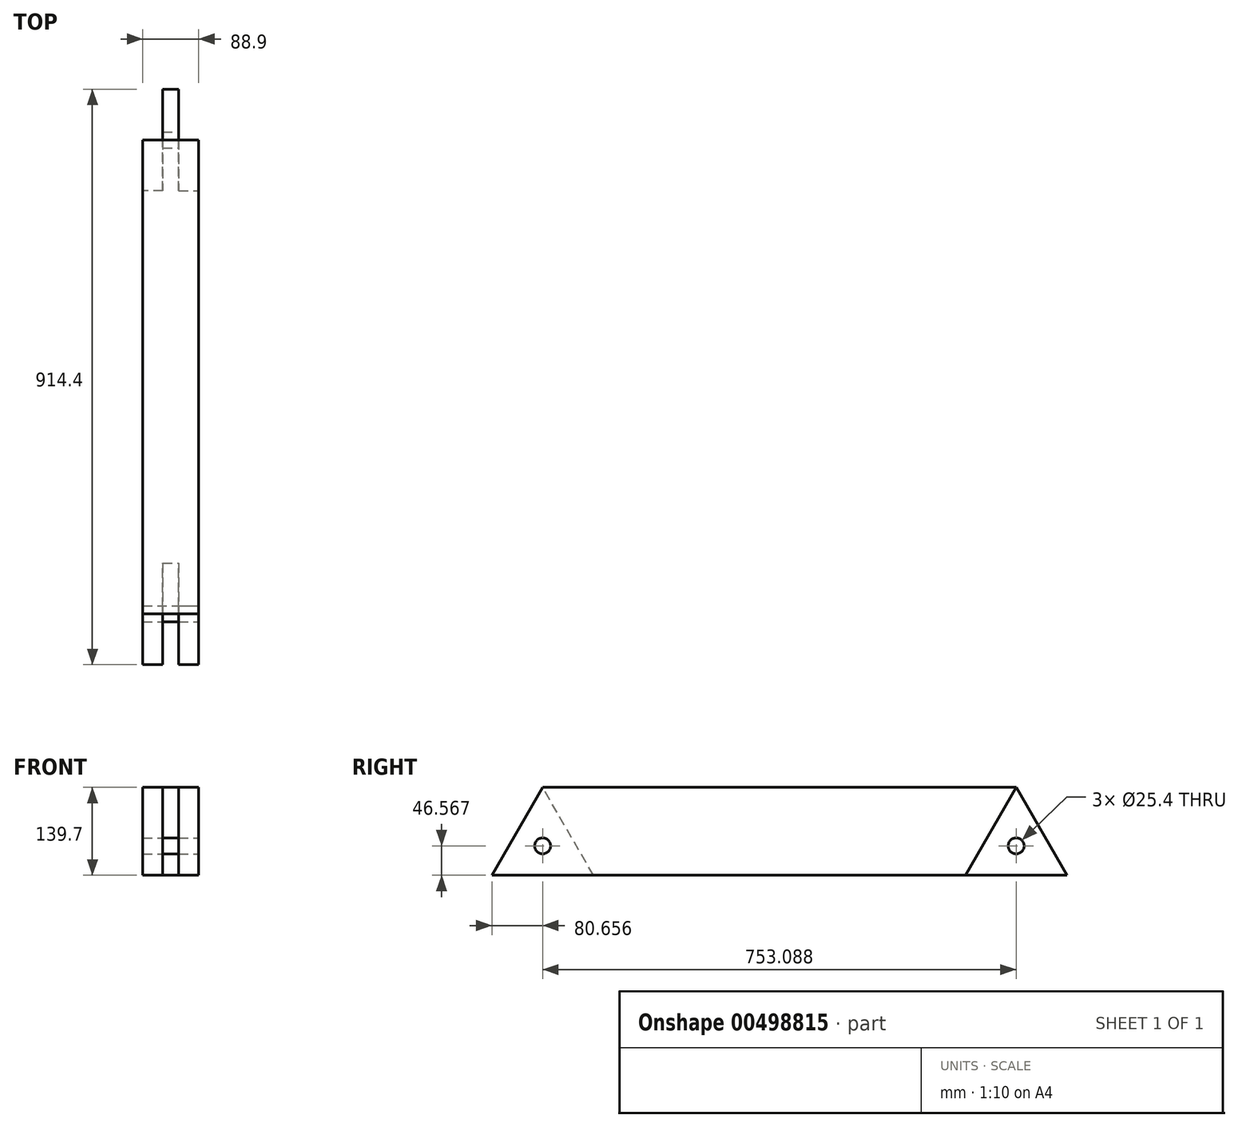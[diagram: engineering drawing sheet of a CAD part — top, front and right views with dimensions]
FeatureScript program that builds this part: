
annotation { "Feature Type Name" : "Feature", "Feature Type Description" : "" }
export const myFeature = defineFeature(function(context is Context, id is Id, definition is map)
    precondition{}
    {
        {
            var Q0;
            Q0=qCreatedBy(makeId("Right.planeOp"),FACE);
            var sketch = newSketch(context, id + "F0", { "sketchPlane" : qUnion([Q0])});
            skLineSegment(sketch, "E0.bottom", {"start": v(-376.54, 69.85) * mm, "end": v(376.54, 69.85) * mm});
            skLineSegment(sketch, "E0.top", {"start": v(-457.2, -69.85) * mm, "end": v(457.2, -69.85) * mm});
            skLineSegment(sketch, "E1", {"start": v(-457.2, -69.85) * mm, "end": v(-376.54, 69.85) * mm});
            skLineSegment(sketch, "E2", {"start": v(376.54, 69.85) * mm, "end": v(457.2, -69.85) * mm});
            skLineSegment(sketch, "E3", {"start": v(-376.54, 69.85) * mm, "end": v(-295.89, -69.85) * mm, "construction": true});
            skLineSegment(sketch, "E4", {"start": v(-295.89, -69.85) * mm, "end": v(-457.2, -69.85) * mm, "construction": true});
            skSolve(sketch);
        }
        {
            var Q0;
            Q0=makeQuery(id+"F0.imprint","IMPRINT",FACE,{"disambiguationData":[TD([[makeQuery(id+"F0.imprint","IMPRINT",EDGE,{"derivedFrom":sQuery(id+"F0.wireOp",EDGE,"E0.bottom")}),-1.0]])]});
            extrude(context, id + "F1", {"entities" : qUnion([Q0]), "depth" : 44.45 * mm, "hasSecondDirection" : true, "secondDirectionOppositeDirection" : true, "secondDirectionDepth" : 44.45 * mm});
        }
        {
            var Q0;
            Q0=qCreatedBy(makeId("Right.planeOp"),FACE);
            var sketch = newSketch(context, id + "F2", { "sketchPlane" : qUnion([Q0])});
            skLineSegment(sketch, "E5", {"start": v(-376.54, 69.85) * mm, "end": v(-457.2, -69.85) * mm});
            skLineSegment(sketch, "E6", {"start": v(-457.2, -69.85) * mm, "end": v(-295.89, -69.85) * mm});
            skLineSegment(sketch, "E7", {"start": v(-295.89, -69.85) * mm, "end": v(-376.54, 69.85) * mm});
            skSolve(sketch);
        }
        {
            var Q0;
            Q0 = qSketchRegion(id + "F2", true);
            extrude(context, id + "F3", {"entities" : qUnion([Q0]), "operationType" : NewBodyOperationType.REMOVE, "oppositeDirection" : true, "depth" : 12.7 * mm, "hasSecondDirection" : true, "secondDirectionOppositeDirection" : false, "secondDirectionDepth" : 12.7 * mm});
        }
        {
            var Q0;
            Q0=makeQuery(id+"F1.opExtrude","CAP_FACE",FACE,{"disambiguationData":[OSD([sQuery(id+"F0.wireOp",EDGE,"E0.bottom"),sQuery(id+"F0.wireOp",EDGE,"E0.top"),sQuery(id+"F0.wireOp",EDGE,"E1"),sQuery(id+"F0.wireOp",EDGE,"E2")])],"isStart":false});
            var sketch = newSketch(context, id + "F4", { "sketchPlane" : qUnion([Q0])});
            skLineSegment(sketch, "E8", {"start": v(376.54, 69.85) * mm, "end": v(457.2, -69.85) * mm});
            skLineSegment(sketch, "E9", {"start": v(376.54, 69.85) * mm, "end": v(295.89, -69.85) * mm});
            skLineSegment(sketch, "E10", {"start": v(295.89, -69.85) * mm, "end": v(457.2, -69.85) * mm});
            skSolve(sketch);
        }
        {
            var Q0;
            Q0 = qSketchRegion(id + "F4", true);
            extrude(context, id + "F5", {"entities" : qUnion([Q0]), "operationType" : NewBodyOperationType.REMOVE, "oppositeDirection" : true, "depth" : 31.75 * mm});
        }
        {
            var Q0;
            Q0=makeQuery(id+"F1.opExtrude","CAP_FACE",FACE,{"disambiguationData":[OSD([sQuery(id+"F0.wireOp",EDGE,"E0.bottom"),sQuery(id+"F0.wireOp",EDGE,"E0.top"),sQuery(id+"F0.wireOp",EDGE,"E1"),sQuery(id+"F0.wireOp",EDGE,"E2")])],"isStart":true});
            var sketch = newSketch(context, id + "F6", { "sketchPlane" : qUnion([Q0])});
            skLineSegment(sketch, "E11", {"start": v(-376.54, 69.85) * mm, "end": v(-457.2, -69.85) * mm});
            skLineSegment(sketch, "E12", {"start": v(-376.54, 69.85) * mm, "end": v(-295.89, -69.85) * mm});
            skLineSegment(sketch, "E13", {"start": v(-295.89, -69.85) * mm, "end": v(-457.2, -69.85) * mm});
            skSolve(sketch);
        }
        {
            var Q0;
            Q0 = qSketchRegion(id + "F6", true);
            extrude(context, id + "F7", {"entities" : qUnion([Q0]), "operationType" : NewBodyOperationType.REMOVE, "oppositeDirection" : true, "depth" : 31.75 * mm});
        }
        {
            var Q0;
            Q0=qCreatedBy(makeId("Right.planeOp"),FACE);
            var sketch = newSketch(context, id + "F8", { "sketchPlane" : qUnion([Q0])});
            skLineSegment(sketch, "E14", {"start": v(-376.54, 69.85) * mm, "end": v(-457.2, -69.85) * mm, "construction": true});
            skLineSegment(sketch, "E15", {"start": v(-457.2, -69.85) * mm, "end": v(-295.89, -69.85) * mm, "construction": true});
            skLineSegment(sketch, "E16", {"start": v(-295.89, -69.85) * mm, "end": v(-376.54, 69.85) * mm, "construction": true});
            skLineSegment(sketch, "E17", {"start": v(-376.54, 69.85) * mm, "end": v(-376.54, -69.85) * mm, "construction": true});
            skLineSegment(sketch, "E18", {"start": v(-457.2, -69.85) * mm, "end": v(-336.22, 0) * mm, "construction": true});
            skCircle(sketch, "E19", {"center": v(-376.54, -23.28) * mm, "radius": 12.7 * mm});
            skLineSegment(sketch, "E20", {"start": v(457.2, -69.85) * mm, "end": v(376.54, 69.85) * mm, "construction": true});
            skLineSegment(sketch, "E21", {"start": v(376.54, 69.85) * mm, "end": v(295.89, -69.85) * mm, "construction": true});
            skLineSegment(sketch, "E22", {"start": v(295.89, -69.85) * mm, "end": v(457.2, -69.85) * mm, "construction": true});
            skLineSegment(sketch, "E23", {"start": v(457.2, -69.85) * mm, "end": v(336.22, 0) * mm, "construction": true});
            skLineSegment(sketch, "E24", {"start": v(376.54, 69.85) * mm, "end": v(376.54, -69.85) * mm, "construction": true});
            skCircle(sketch, "E25", {"center": v(376.54, -23.28) * mm, "radius": 12.7 * mm});
            skSolve(sketch);
        }
        {
            var Q0;
            Q0 = qSketchRegion(id + "F8", true);
            extrude(context, id + "F9", {"entities" : qUnion([Q0]), "operationType" : NewBodyOperationType.REMOVE, "endBound" : BoundingType.THROUGH_ALL, "oppositeDirection" : true, "depth" : 25.4 * mm, "hasSecondDirection" : true, "secondDirectionBound" : BoundingType.THROUGH_ALL, "secondDirectionOppositeDirection" : false, "secondDirectionDepth" : 25.4 * mm});
        }
        {
            var Q0;
            Q0=makeQuery(id+"F1.opExtrude","CAP_FACE",FACE,{"disambiguationData":[OSD([sQuery(id+"F0.wireOp",EDGE,"E0.bottom"),sQuery(id+"F0.wireOp",EDGE,"E0.top"),sQuery(id+"F0.wireOp",EDGE,"E1"),sQuery(id+"F0.wireOp",EDGE,"E2")])],"isStart":false});
            var sketch = newSketch(context, id + "F10", { "sketchPlane" : qUnion([Q0])});
            skCircle(sketch, "E26", {"center": v(-376.54, -23.28) * mm, "radius": 12.7 * mm});
            skSolve(sketch);
        }
        {
            var Q0;
            Q0=makeQuery(id+"F10.imprint","IMPRINT",FACE,{"disambiguationData":[TD([[makeQuery(id+"F10.imprint","IMPRINT",EDGE,{"derivedFrom":sQuery(id+"F10.wireOp",EDGE,"E26")}),1.0]])]});
            extrude(context, id + "F11", {"entities" : qUnion([Q0]), "oppositeDirection" : true, "depth" : 88.9 * mm});
        }
    });
